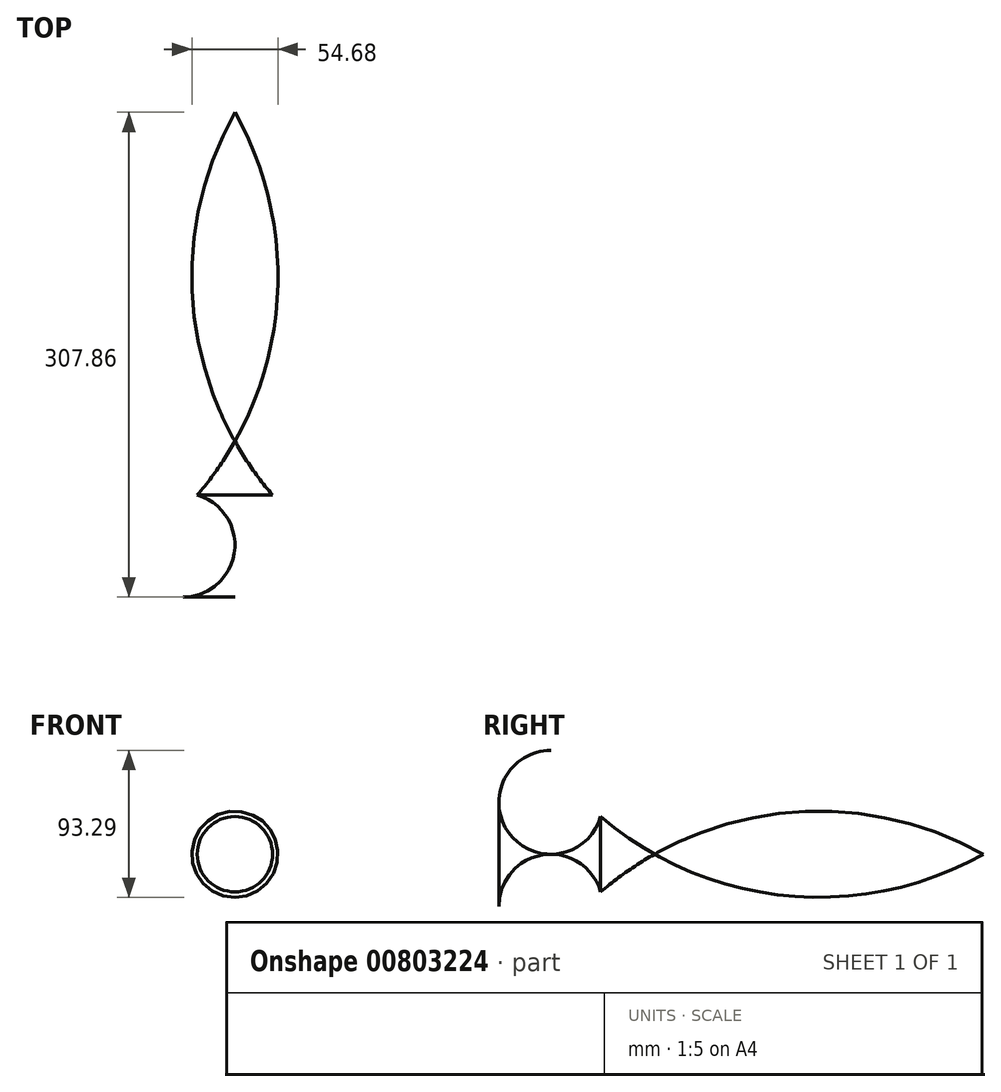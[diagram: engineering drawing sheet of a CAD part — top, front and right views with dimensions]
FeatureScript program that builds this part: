
annotation { "Feature Type Name" : "Feature", "Feature Type Description" : "" }
export const myFeature = defineFeature(function(context is Context, id is Id, definition is map)
    precondition{}
    {
        {
            var Q0;
            Q0=qCreatedBy(makeId("Top.planeOp"),FACE);
            var sketch = newSketch(context, id + "F0", { "sketchPlane" : qUnion([Q0])});
            skLineSegment(sketch, "E0", {"start": v(0, 64.16) * mm, "end": v(0, -74.73) * mm, "construction": true});
            skArc(sketch, "E1", {"start": v(23.9, 0) * mm, "mid": v(6.64, -11.85) * mm, "end": v(0, -31.7) * mm});
            skArc(sketch, "E2", {"start": v(0, 34.22) * mm, "mid": v(11.11, 16.52) * mm, "end": v(23.9, 0) * mm});
            skLineSegment(sketch, "E3", {"start": v(0, 34.22) * mm, "end": v(0, -31.7) * mm});
            skSolve(sketch);
        }
        {
            var Q0;
            {var subQ0=sQuery(id+"F0.wireOp",EDGE,"E1");Q0=makeQuery(id+"F0.imprint","IMPRINT",FACE,{"disambiguationData":[TD([[makeQuery(id+"F0.imprint","IMPRINT",EDGE,{"derivedFrom":subQ0}),-1.0]])]});}
            var Q1;
            Q1=sQuery(id+"F0.wireOp",EDGE,"E0");
            revolve(context, id + "F1", {"surfaceOperationType" : NewSurfaceOperationType.NEW, "entities" : qUnion([Q0]), "axis" : qUnion([Q1]), "revolveType" : RevolveType.FULL});
        }
    });
